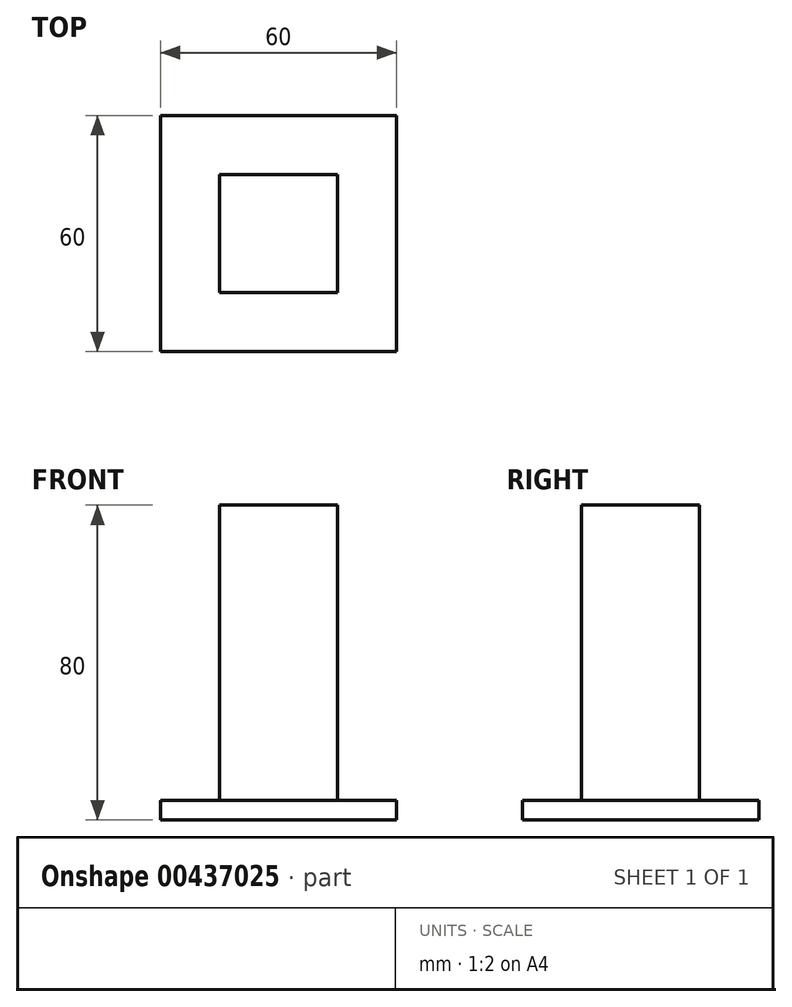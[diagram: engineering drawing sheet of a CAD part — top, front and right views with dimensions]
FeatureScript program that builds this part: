
annotation { "Feature Type Name" : "Feature", "Feature Type Description" : "" }
export const myFeature = defineFeature(function(context is Context, id is Id, definition is map)
    precondition{}
    {
        {
            var Q0;
            Q0=qCreatedBy(makeId("Top.planeOp"),FACE);
            var sketch = newSketch(context, id + "F0", { "sketchPlane" : qUnion([Q0])});
            skLineSegment(sketch, "E0.bottom", {"start": v(0, 0) * mm, "end": v(-60, 0) * mm});
            skLineSegment(sketch, "E0.top", {"start": v(0, 60) * mm, "end": v(-60, 60) * mm});
            skLineSegment(sketch, "E0.left", {"start": v(0, 0) * mm, "end": v(0, 60) * mm});
            skLineSegment(sketch, "E0.right", {"start": v(-60, 0) * mm, "end": v(-60, 60) * mm});
            skSolve(sketch);
        }
        {
            var Q0;
            Q0 = qSketchRegion(id + "F0", true);
            extrude(context, id + "F1", {"entities" : qUnion([Q0]), "depth" : 5 * mm});
        }
        {
            var Q0;
            Q0=makeQuery(id+"F1.opExtrude","CAP_FACE",FACE,{"disambiguationData":[OSD([sQuery(id+"F0.wireOp",EDGE,"E0.bottom"),sQuery(id+"F0.wireOp",EDGE,"E0.top"),sQuery(id+"F0.wireOp",EDGE,"E0.left"),sQuery(id+"F0.wireOp",EDGE,"E0.right")])],"isStart":false});
            var sketch = newSketch(context, id + "F2", { "sketchPlane" : qUnion([Q0])});
            skLineSegment(sketch, "E1.0", {"start": v(-15, 15) * mm, "end": v(-15, 45) * mm});
            skLineSegment(sketch, "E1.1", {"start": v(-15, 15) * mm, "end": v(-45, 15) * mm});
            skLineSegment(sketch, "E1.2", {"start": v(-45, 15) * mm, "end": v(-45, 45) * mm});
            skLineSegment(sketch, "E1.3", {"start": v(-15, 45) * mm, "end": v(-45, 45) * mm});
            skSolve(sketch);
        }
        {
            var Q0;
            Q0 = qSketchRegion(id + "F2", true);
            extrude(context, id + "F3", {"entities" : qUnion([Q0]), "operationType" : NewBodyOperationType.ADD, "depth" : 75 * mm});
        }
    });
